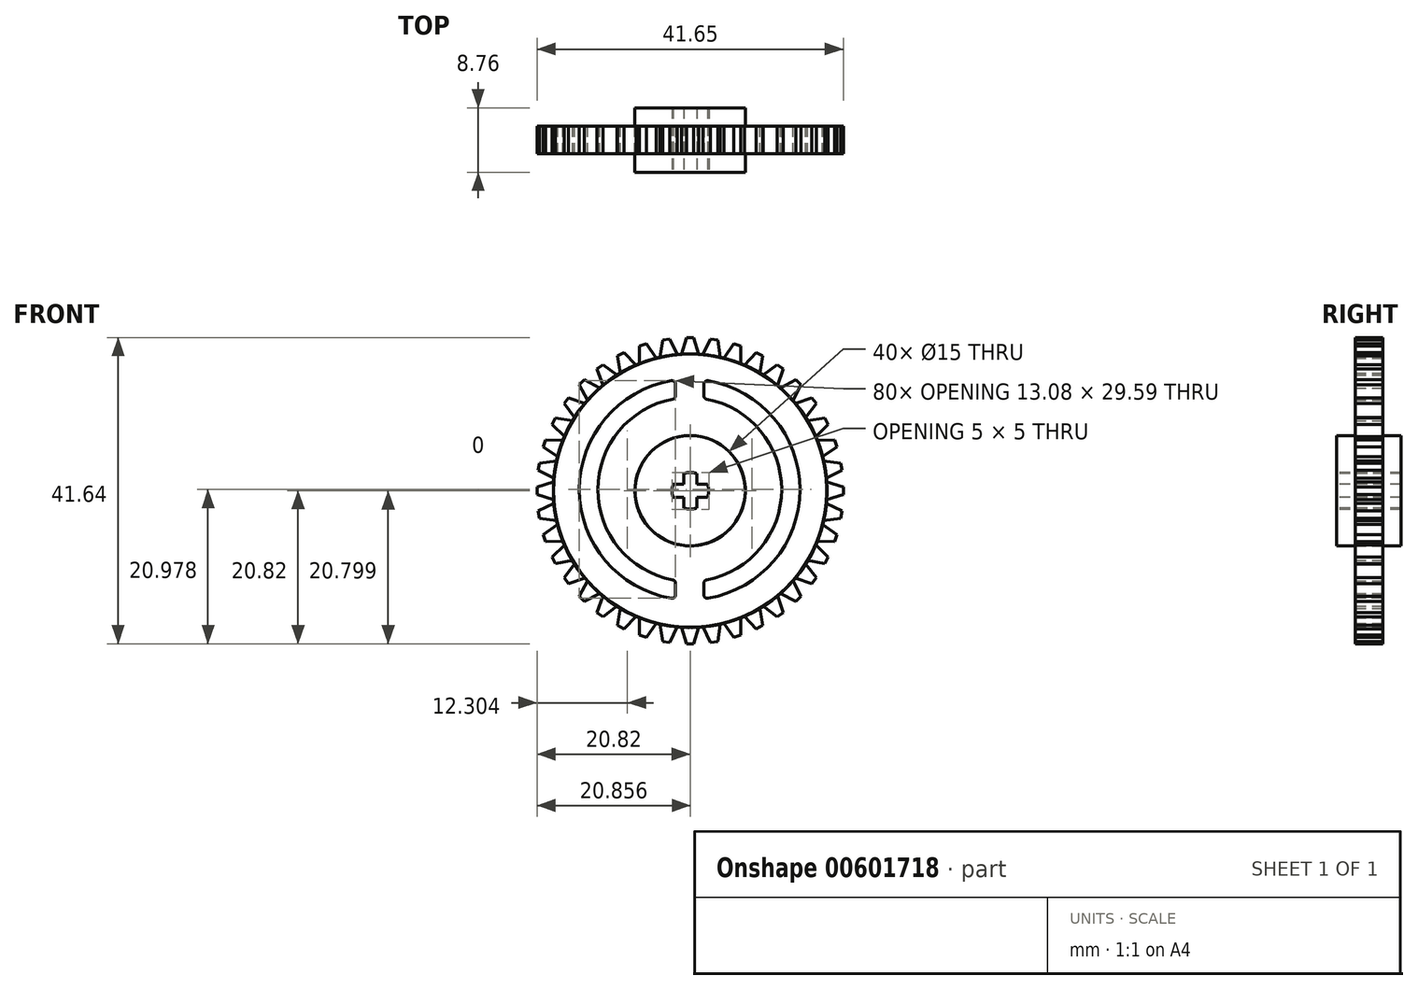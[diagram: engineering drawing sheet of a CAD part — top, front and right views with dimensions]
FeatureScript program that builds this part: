
annotation { "Feature Type Name" : "Feature", "Feature Type Description" : "" }
export const myFeature = defineFeature(function(context is Context, id is Id, definition is map)
    precondition{}
    {
        {
            var Q0;
            Q0=qCreatedBy(makeId("Front.planeOp"),FACE);
            var sketch = newSketch(context, id + "F0", { "sketchPlane" : qUnion([Q0])});
            skCircle(sketch, "E0", {"center": v(0, 0) * mm, "radius": 7.5 * mm});
            skCircle(sketch, "E1", {"center": v(0, 0) * mm, "radius": 18.6 * mm});
            skLineSegment(sketch, "E2", {"start": v(0, 18.6) * mm, "end": v(0, 0) * mm, "construction": true});
            skLineSegment(sketch, "E3", {"start": v(0, 18.6) * mm, "end": v(0, 20.83) * mm});
            skLineSegment(sketch, "E4", {"start": v(0, 20.83) * mm, "end": v(0.5, 20.83) * mm});
            skLineSegment(sketch, "E5", {"start": v(0.5, 20.83) * mm, "end": v(-0.5, 20.83) * mm});
            skLineSegment(sketch, "E6", {"start": v(-0.5, 20.83) * mm, "end": v(-1.19, 18.56) * mm});
            skLineSegment(sketch, "E7.MirrorCS", {"start": v(0.5, 20.83) * mm, "end": v(1.19, 18.56) * mm});
            skSolve(sketch);
        }
        {
            var Q0;
            {var subQ0=sQuery(id+"F0.wireOp",EDGE,"E3");Q0=makeQuery(id+"F0.imprint","IMPRINT",FACE,{"disambiguationData":[TD([[makeQuery(id+"F0.imprint","IMPRINT",EDGE,{"derivedFrom":subQ0}),-1.0]])]});}
            var Q1;
            {var subQ0=sQuery(id+"F0.wireOp",EDGE,"E3");Q1=makeQuery(id+"F0.imprint","IMPRINT",FACE,{"disambiguationData":[TD([[makeQuery(id+"F0.imprint","IMPRINT",EDGE,{"derivedFrom":subQ0}),1.0]])]});}
            var Q2;
            Q2=makeQuery(id+"F0.imprint","IMPRINT",FACE,{"disambiguationData":[TD([[makeQuery(id+"F0.imprint","IMPRINT",EDGE,{"derivedFrom":sQuery(id+"F0.wireOp",EDGE,"E0")}),-1.0]])]});
            extrude(context, id + "F1", {"entities" : qUnion([Q0, Q1, Q2]), "endBound" : BoundingType.SYMMETRIC, "depth" : 3.75 * mm, "offsetDistance" : 25 * mm});
        }
        {
            var Q0;
            Q0=makeQuery(id+"F1.opExtrude","SWEPT_BODY",BODY,{"disambiguationData":[OSD([sQuery(id+"F0.wireOp",EDGE,"E0"),sQuery(id+"F0.wireOp",EDGE,"E1"),sQuery(id+"F0.wireOp",EDGE,"E5"),sQuery(id+"F0.wireOp",EDGE,"E6"),sQuery(id+"F0.wireOp",EDGE,"E7.MirrorCS")])]});
            var Q1;
            Q1=makeQuery(id+"F1.opExtrude","CAP_EDGE",EDGE,{"disambiguationData":[OSD([sQuery(id+"F0.wireOp",EDGE,"E0")])],"isStart":false});
            circularPattern(context, id + "F2", {"entities" : qUnion([Q0]), "axis" : qUnion([Q1]), "angle" : 360 * degree, "instanceCount" : 40, "equalSpace" : true});
        }
        {
            var Q0;
            Q0=makeQuery(id+"F0.imprint","IMPRINT",FACE,{"disambiguationData":[TD([[makeQuery(id+"F0.imprint","IMPRINT",EDGE,{"derivedFrom":sQuery(id+"F0.wireOp",EDGE,"E0")}),1.0]])]});
            extrude(context, id + "F3", {"entities" : qUnion([Q0]), "endBound" : BoundingType.SYMMETRIC, "depth" : 8.75 * mm, "offsetDistance" : 25 * mm});
        }
        {
            var Q0;
            Q0=makeQuery(id+"F3.opExtrude","CAP_FACE",FACE,{"disambiguationData":[OSD([sQuery(id+"F0.wireOp",EDGE,"E0")])],"isStart":false});
            var sketch = newSketch(context, id + "F4", { "sketchPlane" : qUnion([Q0])});
            skCircle(sketch, "E8", {"center": v(0.04, -0.02) * mm, "radius": 2.5 * mm});
            skLineSegment(sketch, "E9", {"start": v(0.94, -0.92) * mm, "end": v(0.94, -2.35) * mm});
            skLineSegment(sketch, "E10", {"start": v(0.94, 0.88) * mm, "end": v(0.94, 2.3) * mm});
            skLineSegment(sketch, "E11", {"start": v(0.94, 0.88) * mm, "end": v(2.37, 0.88) * mm});
            skLineSegment(sketch, "E12", {"start": v(0.94, -0.92) * mm, "end": v(2.37, -0.92) * mm});
            skLineSegment(sketch, "E13", {"start": v(-0.86, -0.92) * mm, "end": v(-0.86, -2.35) * mm});
            skLineSegment(sketch, "E14", {"start": v(-0.86, 0.88) * mm, "end": v(-0.86, 2.3) * mm});
            skLineSegment(sketch, "E15", {"start": v(-0.86, 0.88) * mm, "end": v(-2.3, 0.88) * mm});
            skLineSegment(sketch, "E16", {"start": v(-0.86, -0.92) * mm, "end": v(-2.3, -0.92) * mm});
            skLineSegment(sketch, "E17", {"start": v(0.04, 1.25) * mm, "end": v(0.04, -1.15) * mm, "construction": true});
            skLineSegment(sketch, "E18", {"start": v(-1.26, -0.02) * mm, "end": v(1.3, -0.02) * mm, "construction": true});
            skSolve(sketch);
        }
        {
            var Q0;
            {var subQ4=sQuery(id+"F4.wireOp",EDGE,"E9");Q0=makeQuery(id+"F4.imprint","IMPRINT",FACE,{"disambiguationData":[TD([[makeQuery(id+"F4.imprint","IMPRINT",EDGE,{"derivedFrom":subQ4}),-1.0]])]});}
            extrude(context, id + "F5", {"entities" : qUnion([Q0]), "operationType" : NewBodyOperationType.REMOVE, "endBound" : BoundingType.THROUGH_ALL, "oppositeDirection" : true, "depth" : 25 * mm, "offsetDistance" : 25 * mm});
        }
        {
            var Q0;
            Q0=qCreatedBy(makeId("Front.planeOp"),FACE);
            var sketch = newSketch(context, id + "F6", { "sketchPlane" : qUnion([Q0])});
            skArc(sketch, "E19", {"start": v(-2.56, 14.95) * mm, "mid": v(-15.06, 0.16) * mm, "end": v(-2.56, -14.63) * mm});
            skArc(sketch, "E20", {"start": v(-2.38, 12.44) * mm, "mid": v(-12.56, 0.16) * mm, "end": v(-2.38, -12.12) * mm});
            skLineSegment(sketch, "E21", {"start": v(1.86, -14.14) * mm, "end": v(1.86, -12.62) * mm});
            skLineSegment(sketch, "E22", {"start": v(-1.97, -14.14) * mm, "end": v(-1.97, -12.62) * mm});
            skLineSegment(sketch, "E23", {"start": v(-1.97, 14.45) * mm, "end": v(-1.97, 12.93) * mm});
            skLineSegment(sketch, "E24", {"start": v(1.86, 14.45) * mm, "end": v(1.86, 12.93) * mm});
            skArc(sketch, "E25.trimOffspring", {"start": v(2.27, -12.12) * mm, "mid": v(12.44, 0.16) * mm, "end": v(2.27, 12.44) * mm});
            skArc(sketch, "E26.trimOffspring", {"start": v(2.44, -14.63) * mm, "mid": v(14.94, 0.16) * mm, "end": v(2.44, 14.95) * mm});
            skPoint(sketch, "E27.visualSharp", {"position": v(-1.97, -12.2) * mm});
            skArc(sketch, "E27.filletArc", {"start": v(-1.97, -12.62) * mm, "mid": v(-2.09, -12.3) * mm, "end": v(-2.38, -12.12) * mm});
            skPoint(sketch, "E28.visualSharp", {"position": v(-1.97, -14.72) * mm});
            skArc(sketch, "E28.filletArc", {"start": v(-2.56, -14.63) * mm, "mid": v(-2.15, -14.52) * mm, "end": v(-1.97, -14.14) * mm});
            skPoint(sketch, "E29.visualSharp", {"position": v(1.86, -12.2) * mm});
            skArc(sketch, "E29.filletArc", {"start": v(2.27, -12.12) * mm, "mid": v(1.98, -12.3) * mm, "end": v(1.86, -12.62) * mm});
            skPoint(sketch, "E30.visualSharp", {"position": v(1.86, -14.72) * mm});
            skArc(sketch, "E30.filletArc", {"start": v(1.86, -14.14) * mm, "mid": v(2.04, -14.52) * mm, "end": v(2.44, -14.63) * mm});
            skPoint(sketch, "E31.visualSharp", {"position": v(-1.97, 15.03) * mm});
            skArc(sketch, "E31.filletArc", {"start": v(-1.97, 14.45) * mm, "mid": v(-2.15, 14.84) * mm, "end": v(-2.56, 14.95) * mm});
            skPoint(sketch, "E32.visualSharp", {"position": v(-1.97, 12.5) * mm});
            skArc(sketch, "E32.filletArc", {"start": v(-2.38, 12.44) * mm, "mid": v(-2.09, 12.61) * mm, "end": v(-1.97, 12.93) * mm});
            skPoint(sketch, "E33.visualSharp", {"position": v(1.86, 15.03) * mm});
            skArc(sketch, "E33.filletArc", {"start": v(2.44, 14.95) * mm, "mid": v(2.04, 14.84) * mm, "end": v(1.86, 14.45) * mm});
            skPoint(sketch, "E34.visualSharp", {"position": v(1.86, 12.5) * mm});
            skArc(sketch, "E34.filletArc", {"start": v(1.86, 12.93) * mm, "mid": v(1.98, 12.61) * mm, "end": v(2.27, 12.44) * mm});
            skSolve(sketch);
        }
        {
            var Q0;
            Q0 = qSketchRegion(id + "F6", true);
            extrude(context, id + "F7", {"entities" : qUnion([Q0]), "operationType" : NewBodyOperationType.REMOVE, "endBound" : BoundingType.SYMMETRIC, "oppositeDirection" : true, "depth" : 26.5 * mm, "offsetDistance" : 25 * mm});
        }
    });
